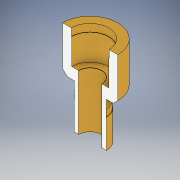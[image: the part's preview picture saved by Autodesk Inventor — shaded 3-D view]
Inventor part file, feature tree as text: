
AUTODESK INVENTOR PART (.ipt)
format: ipt  version: 2018 (Build 220112000, 112)  size: 166,912 bytes
history: native  units: in
note: dims shown in document units (in); Inventor stores cm internally (conversion verified against a paired STEP export)
features: sketch x7, extrude x4, hole x2, revolve x1, chamfer x1
ambient origin geometry x8: Origin, YZ Plane, XZ Plane, XY Plane, X Axis, Y Axis, Z Axis, Center Point
bodies: Solid1 (feature_tree)
feature tree (15):
  extrude  "Extrusion1"  Depth=1.2in TaperAngle=0.0deg
  hole  "Hole1"  [1 undecoded]
  hole  "Hole2"  [1 undecoded]
  extrude  "Extrusion3"  Depth=0.1in
  extrude  "Extrusion4"  Depth=0.6in
  extrude  "Extrusion5"  TaperAngle=90.0deg  [1 undecoded]
  revolve  "Revolution1"  [1 undecoded]
  chamfer  "Chamfer2"  Distance=0.1in
  sketch  "Sketch1"  dims[d0=0.75in d1=1.2in d2=0.0in]
  sketch  "Sketch3"  dims[d6=0.3125in d7=0.75in d8=0.375in d9=0.25in d10=0.5635in d11=1.0in d12=0.8108in]
  sketch  "Sketch4"  dims[d13=0.4844in d14=0.75in d15=0.375in d16=0.25in d17=0.5635in d18=0.4in d19=0.8108in d20=0.501in]
  sketch  "Sketch5"  dims[d21=0.45in d22=0.0in d23=0.51in]
  sketch  "Sketch6"  dims[d24=0.1in d25=0.0in d26=0.439in]
  sketch  "Sketch7"  dims[d27=0.6in d28=0.0in d35=0.44in]
  sketch  "Sketch9"  dims[d36=90.0deg d38=90.0deg d39=0.01in d40=0.1in d41=90.0deg d42=0.0625in d43=0.125in d44=45.0deg d45=1.0in d46=1.0in]
note: 4 required parameter values undecoded (feature->parameter linkage not recoverable at this tier; creation-order binding heuristic only, values carry confidence <= 0.55)